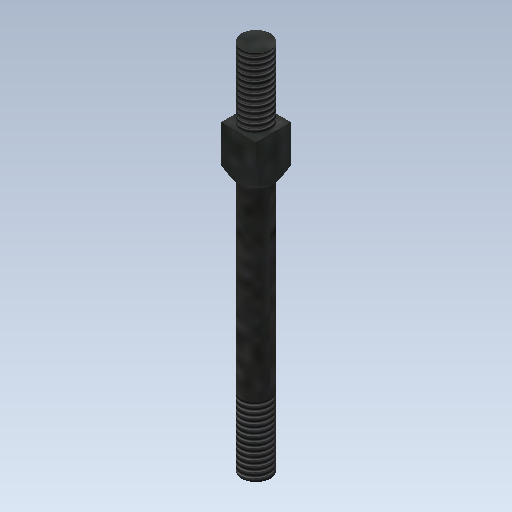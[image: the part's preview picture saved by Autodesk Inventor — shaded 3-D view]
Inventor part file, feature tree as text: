
AUTODESK INVENTOR PART (.ipt)
format: ipt  version: 2020 (Build 240168000, 168)  size: 137,216 bytes
history: native  units: mm
features: sketch x4, extrude x3, thread x2, revolve x1, projected_geometry x1
ambient origin geometry x8: Origin, YZ Plane, XZ Plane, XY Plane, X Axis, Y Axis, Z Axis, Center Point
bodies: Solid1 (feature_tree)
feature tree (11):
  extrude  "Extrusion1"  Depth=3.0mm
  extrude  "Extrusion2"  Depth=2.5mm
  extrude  "Extrusion3"  Depth=2.5mm
  thread  "Thread1"  [1 undecoded]
  thread  "Thread2"  [1 undecoded]
  revolve  "Revolution1"  Angle=45.0deg
  sketch  "Sketch1"  dims[d0=3.0mm d1=3.0mm]
  sketch  "Sketch2"  dims[d2=4.1mm d3=0.0mm d4=2.5mm]
  sketch  "Sketch3"  dims[d5=6.0mm d6=0.0mm d7=2.5mm d8=21.9mm d9=0.0mm d10=6.0mm d11=0.0mm]
  sketch  "Sketch4"  dims[d12=10.0mm d13=0.0mm d15=45.0deg d16=90.0deg]
  projected_geometry  "Project Cut Edges1"
note: 2 required parameter values undecoded (feature->parameter linkage not recoverable at this tier; creation-order binding heuristic only, values carry confidence <= 0.55)
